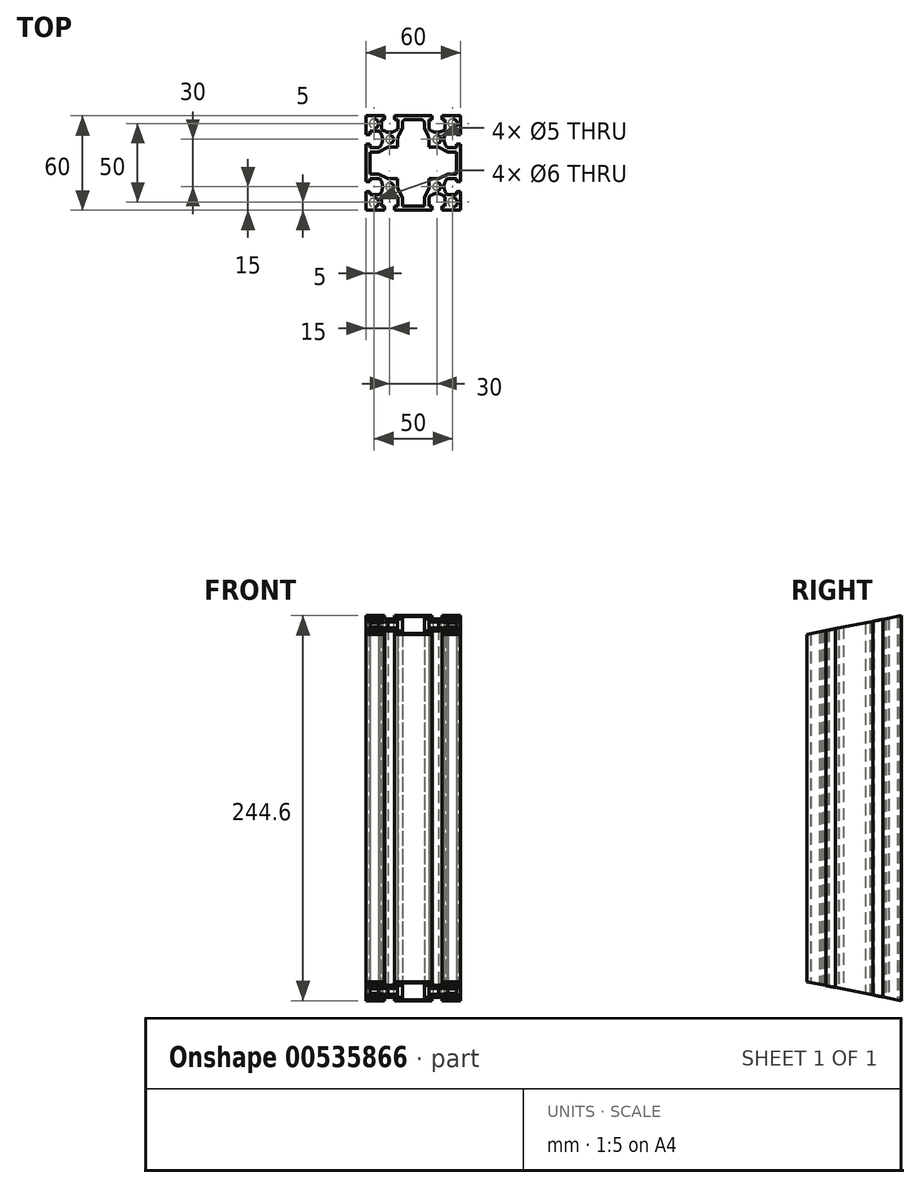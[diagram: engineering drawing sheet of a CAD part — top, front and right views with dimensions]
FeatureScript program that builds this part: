
annotation { "Feature Type Name" : "Feature", "Feature Type Description" : "" }
export const myFeature = defineFeature(function(context is Context, id is Id, definition is map)
    precondition{}
    {
        {
            var Q0;
            Q0=qCreatedBy(makeId("Top.planeOp"),FACE);
            var sketch = newSketch(context, id + "F0", { "sketchPlane" : qUnion([Q0])});
            skLineSegment(sketch, "E0.bottom", {"start": v(30, -30) * mm, "end": v(-30, -30) * mm});
            skLineSegment(sketch, "E0.top", {"start": v(30, 30) * mm, "end": v(-30, 30) * mm});
            skLineSegment(sketch, "E0.left", {"start": v(30, -30) * mm, "end": v(30, 30) * mm});
            skLineSegment(sketch, "E0.right", {"start": v(-30, -30) * mm, "end": v(-30, 30) * mm});
            skPoint(sketch, "E0.middle", {"position": v(0, 0) * mm});
            skLineSegment(sketch, "E1.top", {"start": v(-11.85, 30) * mm, "end": v(-18.15, 30) * mm});
            skLineSegment(sketch, "E1.left", {"start": v(-11.85, 27.5) * mm, "end": v(-11.85, 30) * mm});
            skLineSegment(sketch, "E1.right", {"start": v(-18.15, 27.5) * mm, "end": v(-18.15, 30) * mm});
            skPoint(sketch, "E1.middle", {"position": v(-15, 28.75) * mm});
            skLineSegment(sketch, "E2.bottom", {"start": v(-9.85, 27.5) * mm, "end": v(-11.85, 27.5) * mm});
            skLineSegment(sketch, "E2.left", {"start": v(-9.85, 27.5) * mm, "end": v(-9.85, 21.55) * mm});
            skLineSegment(sketch, "E2.right", {"start": v(-20.15, 27.5) * mm, "end": v(-20.15, 21.55) * mm});
            skPoint(sketch, "E2.middle", {"position": v(-15, 24.52) * mm});
            skArc(sketch, "E3", {"start": v(-20.15, 21.55) * mm, "mid": v(-15, 19.5) * mm, "end": v(-9.85, 21.55) * mm});
            skPoint(sketch, "E4.MirrorP", {"position": v(15, 24.52) * mm});
            skPoint(sketch, "E5.MirrorP", {"position": v(15, 28.75) * mm});
            skLineSegment(sketch, "E6.MirrorCS", {"start": v(11.85, 27.5) * mm, "end": v(11.85, 30) * mm});
            skLineSegment(sketch, "E7.MirrorCS", {"start": v(18.15, 27.5) * mm, "end": v(18.15, 30) * mm});
            skLineSegment(sketch, "E8.MirrorCS", {"start": v(9.85, 27.5) * mm, "end": v(11.85, 27.5) * mm});
            skLineSegment(sketch, "E9.MirrorCS", {"start": v(9.85, 27.5) * mm, "end": v(9.85, 21.55) * mm});
            skArc(sketch, "E10.MirrorCS", {"start": v(20.15, 21.55) * mm, "mid": v(15, 19.5) * mm, "end": v(9.85, 21.55) * mm});
            skLineSegment(sketch, "E11.MirrorCS", {"start": v(20.15, 27.5) * mm, "end": v(20.15, 21.55) * mm});
            skLineSegment(sketch, "E12.MirrorCS", {"start": v(11.85, 30) * mm, "end": v(18.15, 30) * mm});
            skLineSegment(sketch, "E13.1.0", {"start": v(27.5, 20.15) * mm, "end": v(21.55, 20.15) * mm});
            skLineSegment(sketch, "E13.1.1", {"start": v(27.5, 9.85) * mm, "end": v(21.55, 9.85) * mm});
            skArc(sketch, "E13.1.2", {"start": v(21.55, 20.15) * mm, "mid": v(19.5, 15) * mm, "end": v(21.55, 9.85) * mm});
            skLineSegment(sketch, "E13.1.3", {"start": v(27.5, -9.85) * mm, "end": v(21.55, -9.85) * mm});
            skLineSegment(sketch, "E13.1.4", {"start": v(27.5, -20.15) * mm, "end": v(21.55, -20.15) * mm});
            skPoint(sketch, "E13.1.5", {"position": v(28.75, 15) * mm});
            skPoint(sketch, "E13.1.6", {"position": v(28.75, -15) * mm});
            skArc(sketch, "E13.1.7", {"start": v(21.55, -20.15) * mm, "mid": v(19.5, -15) * mm, "end": v(21.55, -9.85) * mm});
            skPoint(sketch, "E13.1.8", {"position": v(24.52, -15) * mm});
            skPoint(sketch, "E13.1.9", {"position": v(24.52, 15) * mm});
            skLineSegment(sketch, "E13.1.10", {"start": v(27.5, 9.85) * mm, "end": v(27.5, 20.15) * mm});
            skLineSegment(sketch, "E13.1.11", {"start": v(27.5, -11.85) * mm, "end": v(27.5, -18.15) * mm});
            skLineSegment(sketch, "E13.1.12", {"start": v(30, 11.85) * mm, "end": v(30, 18.15) * mm});
            skLineSegment(sketch, "E13.1.13", {"start": v(30, -11.85) * mm, "end": v(30, -18.15) * mm});
            skLineSegment(sketch, "E13.1.14", {"start": v(27.5, 18.15) * mm, "end": v(30, 18.15) * mm});
            skLineSegment(sketch, "E13.1.15", {"start": v(27.5, 11.85) * mm, "end": v(30, 11.85) * mm});
            skLineSegment(sketch, "E13.1.16", {"start": v(27.5, 11.85) * mm, "end": v(27.5, 18.15) * mm});
            skLineSegment(sketch, "E13.1.17", {"start": v(27.5, -9.85) * mm, "end": v(27.5, -20.15) * mm});
            skLineSegment(sketch, "E13.1.18", {"start": v(27.5, -18.15) * mm, "end": v(30, -18.15) * mm});
            skLineSegment(sketch, "E13.1.19", {"start": v(27.5, -11.85) * mm, "end": v(30, -11.85) * mm});
            skLineSegment(sketch, "E13.2.0", {"start": v(20.15, -27.5) * mm, "end": v(20.15, -21.55) * mm});
            skLineSegment(sketch, "E13.2.1", {"start": v(9.85, -27.5) * mm, "end": v(9.85, -21.55) * mm});
            skArc(sketch, "E13.2.2", {"start": v(20.15, -21.55) * mm, "mid": v(15, -19.5) * mm, "end": v(9.85, -21.55) * mm});
            skLineSegment(sketch, "E13.2.3", {"start": v(-9.85, -27.5) * mm, "end": v(-9.85, -21.55) * mm});
            skLineSegment(sketch, "E13.2.4", {"start": v(-20.15, -27.5) * mm, "end": v(-20.15, -21.55) * mm});
            skPoint(sketch, "E13.2.5", {"position": v(15, -28.75) * mm});
            skPoint(sketch, "E13.2.6", {"position": v(-15, -28.75) * mm});
            skArc(sketch, "E13.2.7", {"start": v(-20.15, -21.55) * mm, "mid": v(-15, -19.5) * mm, "end": v(-9.85, -21.55) * mm});
            skPoint(sketch, "E13.2.8", {"position": v(-15, -24.52) * mm});
            skPoint(sketch, "E13.2.9", {"position": v(15, -24.52) * mm});
            skLineSegment(sketch, "E13.2.10", {"start": v(9.85, -27.5) * mm, "end": v(20.15, -27.5) * mm});
            skLineSegment(sketch, "E13.2.11", {"start": v(-11.85, -27.5) * mm, "end": v(-18.15, -27.5) * mm});
            skLineSegment(sketch, "E13.2.12", {"start": v(11.85, -30) * mm, "end": v(18.15, -30) * mm});
            skLineSegment(sketch, "E13.2.13", {"start": v(-11.85, -30) * mm, "end": v(-18.15, -30) * mm});
            skLineSegment(sketch, "E13.2.14", {"start": v(18.15, -27.5) * mm, "end": v(18.15, -30) * mm});
            skLineSegment(sketch, "E13.2.15", {"start": v(11.85, -27.5) * mm, "end": v(11.85, -30) * mm});
            skLineSegment(sketch, "E13.2.16", {"start": v(11.85, -27.5) * mm, "end": v(18.15, -27.5) * mm});
            skLineSegment(sketch, "E13.2.17", {"start": v(-9.85, -27.5) * mm, "end": v(-20.15, -27.5) * mm});
            skLineSegment(sketch, "E13.2.18", {"start": v(-18.15, -27.5) * mm, "end": v(-18.15, -30) * mm});
            skLineSegment(sketch, "E13.2.19", {"start": v(-11.85, -27.5) * mm, "end": v(-11.85, -30) * mm});
            skLineSegment(sketch, "E13.3.0", {"start": v(-27.5, -20.15) * mm, "end": v(-21.55, -20.15) * mm});
            skLineSegment(sketch, "E13.3.1", {"start": v(-27.5, -9.85) * mm, "end": v(-21.55, -9.85) * mm});
            skArc(sketch, "E13.3.2", {"start": v(-21.55, -20.15) * mm, "mid": v(-19.5, -15) * mm, "end": v(-21.55, -9.85) * mm});
            skLineSegment(sketch, "E13.3.3", {"start": v(-27.5, 9.85) * mm, "end": v(-21.55, 9.85) * mm});
            skLineSegment(sketch, "E13.3.4", {"start": v(-27.5, 20.15) * mm, "end": v(-21.55, 20.15) * mm});
            skPoint(sketch, "E13.3.5", {"position": v(-28.75, -15) * mm});
            skPoint(sketch, "E13.3.6", {"position": v(-28.75, 15) * mm});
            skArc(sketch, "E13.3.7", {"start": v(-21.55, 20.15) * mm, "mid": v(-19.5, 15) * mm, "end": v(-21.55, 9.85) * mm});
            skPoint(sketch, "E13.3.8", {"position": v(-24.52, 15) * mm});
            skPoint(sketch, "E13.3.9", {"position": v(-24.52, -15) * mm});
            skLineSegment(sketch, "E13.3.10", {"start": v(-27.5, -9.85) * mm, "end": v(-27.5, -20.15) * mm});
            skLineSegment(sketch, "E13.3.11", {"start": v(-27.5, 11.85) * mm, "end": v(-27.5, 18.15) * mm});
            skLineSegment(sketch, "E13.3.12", {"start": v(-30, -11.85) * mm, "end": v(-30, -18.15) * mm});
            skLineSegment(sketch, "E13.3.13", {"start": v(-30, 11.85) * mm, "end": v(-30, 18.15) * mm});
            skLineSegment(sketch, "E13.3.14", {"start": v(-27.5, -18.15) * mm, "end": v(-30, -18.15) * mm});
            skLineSegment(sketch, "E13.3.15", {"start": v(-27.5, -11.85) * mm, "end": v(-30, -11.85) * mm});
            skLineSegment(sketch, "E13.3.16", {"start": v(-27.5, -11.85) * mm, "end": v(-27.5, -18.15) * mm});
            skLineSegment(sketch, "E13.3.17", {"start": v(-27.5, 9.85) * mm, "end": v(-27.5, 20.15) * mm});
            skLineSegment(sketch, "E13.3.18", {"start": v(-27.5, 18.15) * mm, "end": v(-30, 18.15) * mm});
            skLineSegment(sketch, "E13.3.19", {"start": v(-27.5, 11.85) * mm, "end": v(-30, 11.85) * mm});
            skLineSegment(sketch, "E13.anchor1", {"start": v(0, 0) * mm, "end": v(-20.15, 21.55) * mm, "construction": true});
            skLineSegment(sketch, "E13.anchor2", {"start": v(0, 0) * mm, "end": v(-21.55, -20.15) * mm, "construction": true});
            skLineSegment(sketch, "E14.trimOffspring", {"start": v(-18.15, 27.5) * mm, "end": v(-20.15, 27.5) * mm});
            skLineSegment(sketch, "E15.trimOffspring", {"start": v(18.15, 27.5) * mm, "end": v(20.15, 27.5) * mm});
            skCircle(sketch, "E16", {"center": v(-15, 15) * mm, "radius": 2.5 * mm});
            skCircle(sketch, "E17", {"center": v(-25, 25) * mm, "radius": 3 * mm});
            skCircle(sketch, "E18.MirrorC", {"center": v(25, 25) * mm, "radius": 3 * mm});
            skCircle(sketch, "E19.MirrorC", {"center": v(25, -25) * mm, "radius": 3 * mm});
            skCircle(sketch, "E20.MirrorC", {"center": v(-25, -25) * mm, "radius": 3 * mm});
            skCircle(sketch, "E21.MirrorC", {"center": v(15, 15) * mm, "radius": 2.5 * mm});
            skCircle(sketch, "E22.MirrorC", {"center": v(15, -15) * mm, "radius": 2.5 * mm});
            skCircle(sketch, "E23.MirrorC", {"center": v(-15, -15) * mm, "radius": 2.5 * mm});
            skLineSegment(sketch, "E24", {"start": v(-7, 27.5) * mm, "end": v(0, 27.5) * mm});
            skLineSegment(sketch, "E25", {"start": v(-7, 27.5) * mm, "end": v(-7, 22) * mm});
            skLineSegment(sketch, "E26", {"start": v(-10, 10) * mm, "end": v(-10, 16) * mm});
            skLineSegment(sketch, "E27", {"start": v(-10, 16) * mm, "end": v(-7, 22) * mm});
            skLineSegment(sketch, "E28.MirrorCS", {"start": v(10, 10) * mm, "end": v(10, 16) * mm});
            skLineSegment(sketch, "E29.MirrorCS", {"start": v(10, 16) * mm, "end": v(7, 22) * mm});
            skLineSegment(sketch, "E30.MirrorCS", {"start": v(7, 27.5) * mm, "end": v(0, 27.5) * mm});
            skLineSegment(sketch, "E31.MirrorCS", {"start": v(7, 27.5) * mm, "end": v(7, 22) * mm});
            skLineSegment(sketch, "E32.1.0", {"start": v(-10, -10) * mm, "end": v(-16, -10) * mm});
            skLineSegment(sketch, "E32.1.1", {"start": v(-16, -10) * mm, "end": v(-22, -7) * mm});
            skLineSegment(sketch, "E32.1.2", {"start": v(-27.5, -7) * mm, "end": v(-22, -7) * mm});
            skLineSegment(sketch, "E32.1.3", {"start": v(-27.5, -7) * mm, "end": v(-27.5, 0) * mm});
            skLineSegment(sketch, "E32.1.4", {"start": v(-27.5, 7) * mm, "end": v(-27.5, 0) * mm});
            skLineSegment(sketch, "E32.1.5", {"start": v(-27.5, 7) * mm, "end": v(-22, 7) * mm});
            skLineSegment(sketch, "E32.1.6", {"start": v(-16, 10) * mm, "end": v(-22, 7) * mm});
            skLineSegment(sketch, "E32.1.7", {"start": v(-10, 10) * mm, "end": v(-16, 10) * mm});
            skLineSegment(sketch, "E32.2.0", {"start": v(10, -10) * mm, "end": v(10, -16) * mm});
            skLineSegment(sketch, "E32.2.1", {"start": v(10, -16) * mm, "end": v(7, -22) * mm});
            skLineSegment(sketch, "E32.2.2", {"start": v(7, -27.5) * mm, "end": v(7, -22) * mm});
            skLineSegment(sketch, "E32.2.3", {"start": v(7, -27.5) * mm, "end": v(0, -27.5) * mm});
            skLineSegment(sketch, "E32.2.4", {"start": v(-7, -27.5) * mm, "end": v(0, -27.5) * mm});
            skLineSegment(sketch, "E32.2.5", {"start": v(-7, -27.5) * mm, "end": v(-7, -22) * mm});
            skLineSegment(sketch, "E32.2.6", {"start": v(-10, -16) * mm, "end": v(-7, -22) * mm});
            skLineSegment(sketch, "E32.2.7", {"start": v(-10, -10) * mm, "end": v(-10, -16) * mm});
            skLineSegment(sketch, "E32.3.0", {"start": v(10, 10) * mm, "end": v(16, 10) * mm});
            skLineSegment(sketch, "E32.3.1", {"start": v(16, 10) * mm, "end": v(22, 7) * mm});
            skLineSegment(sketch, "E32.3.2", {"start": v(27.5, 7) * mm, "end": v(22, 7) * mm});
            skLineSegment(sketch, "E32.3.3", {"start": v(27.5, 7) * mm, "end": v(27.5, 0) * mm});
            skLineSegment(sketch, "E32.3.4", {"start": v(27.5, -7) * mm, "end": v(27.5, 0) * mm});
            skLineSegment(sketch, "E32.3.5", {"start": v(27.5, -7) * mm, "end": v(22, -7) * mm});
            skLineSegment(sketch, "E32.3.6", {"start": v(16, -10) * mm, "end": v(22, -7) * mm});
            skLineSegment(sketch, "E32.3.7", {"start": v(10, -10) * mm, "end": v(16, -10) * mm});
            skSolve(sketch);
        }
        {
            var Q0;
            {var subQ30=sQuery(id+"F0.wireOp",EDGE,"E1.left");Q0=makeQuery(id+"F0.imprint","IMPRINT",FACE,{"disambiguationData":[TD([[makeQuery(id+"F0.imprint","IMPRINT",EDGE,{"derivedFrom":subQ30}),-1.0]])]});}
            extrude(context, id + "F1", {"entities" : qUnion([Q0]), "depth" : 244.6 * mm, "offsetDistance" : 25 * mm});
        }
        {
            var Q0;
            Q0=makeQuery(id+"F1.opExtrude","SWEPT_EDGE",EDGE,{"disambiguationData":[OSD([sQuery(id+"F0.wireOp",EDGE,"E24"),sQuery(id+"F0.wireOp",EDGE,"E25")])]});
            var Q1;
            Q1=makeQuery(id+"F1.opExtrude","SWEPT_EDGE",EDGE,{"disambiguationData":[OSD([sQuery(id+"F0.wireOp",EDGE,"E30.MirrorCS"),sQuery(id+"F0.wireOp",EDGE,"E31.MirrorCS")])]});
            var Q2;
            Q2=makeQuery(id+"F1.opExtrude","SWEPT_EDGE",EDGE,{"disambiguationData":[OSD([sQuery(id+"F0.wireOp",EDGE,"840db5bc-c403-45cd-90c7-254e62d9e8c5.3.2"),sQuery(id+"F0.wireOp",EDGE,"840db5bc-c403-45cd-90c7-254e62d9e8c5.3.3")])]});
            var Q3;
            Q3=makeQuery(id+"F1.opExtrude","SWEPT_EDGE",EDGE,{"disambiguationData":[OSD([sQuery(id+"F0.wireOp",EDGE,"840db5bc-c403-45cd-90c7-254e62d9e8c5.3.4"),sQuery(id+"F0.wireOp",EDGE,"840db5bc-c403-45cd-90c7-254e62d9e8c5.3.5")])]});
            var Q4;
            Q4=makeQuery(id+"F1.opExtrude","SWEPT_EDGE",EDGE,{"disambiguationData":[OSD([sQuery(id+"F0.wireOp",EDGE,"840db5bc-c403-45cd-90c7-254e62d9e8c5.1.4"),sQuery(id+"F0.wireOp",EDGE,"840db5bc-c403-45cd-90c7-254e62d9e8c5.1.5")])]});
            var Q5;
            Q5=makeQuery(id+"F1.opExtrude","SWEPT_EDGE",EDGE,{"disambiguationData":[OSD([sQuery(id+"F0.wireOp",EDGE,"840db5bc-c403-45cd-90c7-254e62d9e8c5.1.2"),sQuery(id+"F0.wireOp",EDGE,"840db5bc-c403-45cd-90c7-254e62d9e8c5.1.3")])]});
            var Q6;
            Q6=makeQuery(id+"F1.opExtrude","SWEPT_EDGE",EDGE,{"disambiguationData":[OSD([sQuery(id+"F0.wireOp",EDGE,"840db5bc-c403-45cd-90c7-254e62d9e8c5.2.2"),sQuery(id+"F0.wireOp",EDGE,"840db5bc-c403-45cd-90c7-254e62d9e8c5.2.3")])]});
            var Q7;
            Q7=makeQuery(id+"F1.opExtrude","SWEPT_EDGE",EDGE,{"disambiguationData":[OSD([sQuery(id+"F0.wireOp",EDGE,"840db5bc-c403-45cd-90c7-254e62d9e8c5.2.4"),sQuery(id+"F0.wireOp",EDGE,"840db5bc-c403-45cd-90c7-254e62d9e8c5.2.5")])]});
            fillet(context, id + "F2", {"entities" : qUnion([Q0, Q1, Q2, Q3, Q4, Q5, Q6, Q7]), "radius" : 2 * mm, "tangentPropagation" : true, "allowEdgeOverflow" : false});
        }
        {
            var Q0;
            Q0=makeQuery(id+"F1.opExtrude","SWEPT_EDGE",EDGE,{"disambiguationData":[OSD([sQuery(id+"F0.wireOp",EDGE,"E26"),sQuery(id+"F0.wireOp",EDGE,"E27")])]});
            var Q1;
            Q1=makeQuery(id+"F1.opExtrude","SWEPT_EDGE",EDGE,{"disambiguationData":[OSD([sQuery(id+"F0.wireOp",EDGE,"E28.MirrorCS"),sQuery(id+"F0.wireOp",EDGE,"E29.MirrorCS")])]});
            var Q2;
            Q2=makeQuery(id+"F1.opExtrude","SWEPT_EDGE",EDGE,{"disambiguationData":[OSD([sQuery(id+"F0.wireOp",EDGE,"840db5bc-c403-45cd-90c7-254e62d9e8c5.3.0"),sQuery(id+"F0.wireOp",EDGE,"840db5bc-c403-45cd-90c7-254e62d9e8c5.3.1")])]});
            var Q3;
            Q3=makeQuery(id+"F1.opExtrude","SWEPT_EDGE",EDGE,{"disambiguationData":[OSD([sQuery(id+"F0.wireOp",EDGE,"840db5bc-c403-45cd-90c7-254e62d9e8c5.1.6"),sQuery(id+"F0.wireOp",EDGE,"840db5bc-c403-45cd-90c7-254e62d9e8c5.1.7")])]});
            var Q4;
            Q4=makeQuery(id+"F1.opExtrude","SWEPT_EDGE",EDGE,{"disambiguationData":[OSD([sQuery(id+"F0.wireOp",EDGE,"840db5bc-c403-45cd-90c7-254e62d9e8c5.1.0"),sQuery(id+"F0.wireOp",EDGE,"840db5bc-c403-45cd-90c7-254e62d9e8c5.1.1")])]});
            var Q5;
            Q5=makeQuery(id+"F1.opExtrude","SWEPT_EDGE",EDGE,{"disambiguationData":[OSD([sQuery(id+"F0.wireOp",EDGE,"840db5bc-c403-45cd-90c7-254e62d9e8c5.3.6"),sQuery(id+"F0.wireOp",EDGE,"840db5bc-c403-45cd-90c7-254e62d9e8c5.3.7")])]});
            var Q6;
            Q6=makeQuery(id+"F1.opExtrude","SWEPT_EDGE",EDGE,{"disambiguationData":[OSD([sQuery(id+"F0.wireOp",EDGE,"840db5bc-c403-45cd-90c7-254e62d9e8c5.2.0"),sQuery(id+"F0.wireOp",EDGE,"840db5bc-c403-45cd-90c7-254e62d9e8c5.2.1")])]});
            var Q7;
            Q7=makeQuery(id+"F1.opExtrude","SWEPT_EDGE",EDGE,{"disambiguationData":[OSD([sQuery(id+"F0.wireOp",EDGE,"840db5bc-c403-45cd-90c7-254e62d9e8c5.2.6"),sQuery(id+"F0.wireOp",EDGE,"840db5bc-c403-45cd-90c7-254e62d9e8c5.2.7")])]});
            fillet(context, id + "F3", {"entities" : qUnion([Q0, Q1, Q2, Q3, Q4, Q5, Q6, Q7]), "radius" : 7 * mm, "tangentPropagation" : true, "allowEdgeOverflow" : false});
        }
        {
            var Q0;
            Q0=qCreatedBy(makeId("Right.planeOp"),FACE);
            var sketch = newSketch(context, id + "F4", { "sketchPlane" : qUnion([Q0])});
            skLineSegment(sketch, "E33.bottom", {"start": v(30, 0) * mm, "end": v(-94.02, 24.67) * mm});
            skLineSegment(sketch, "E33.top", {"start": v(6.06, -120.36) * mm, "end": v(-117.96, -95.69) * mm});
            skLineSegment(sketch, "E33.left", {"start": v(30, 0) * mm, "end": v(6.06, -120.36) * mm});
            skLineSegment(sketch, "E33.right", {"start": v(-94.02, 24.67) * mm, "end": v(-117.96, -95.69) * mm});
            skLineSegment(sketch, "E34.bottom", {"start": v(11.53, 337.46) * mm, "end": v(-122.88, 310.72) * mm});
            skLineSegment(sketch, "E34.top", {"start": v(30, 244.6) * mm, "end": v(-104.4, 217.86) * mm});
            skLineSegment(sketch, "E34.left", {"start": v(11.53, 337.46) * mm, "end": v(30, 244.6) * mm});
            skLineSegment(sketch, "E34.right", {"start": v(-122.88, 310.72) * mm, "end": v(-104.4, 217.86) * mm});
            skSolve(sketch);
        }
        {
            var Q0;
            Q0 = qSketchRegion(id + "F4", true);
            extrude(context, id + "F5", {"entities" : qUnion([Q0]), "operationType" : NewBodyOperationType.REMOVE, "oppositeDirection" : true, "depth" : 30 * mm, "offsetDistance" : 25 * mm, "hasSecondDirection" : true, "secondDirectionOppositeDirection" : false, "secondDirectionDepth" : 30 * mm});
        }
    });
